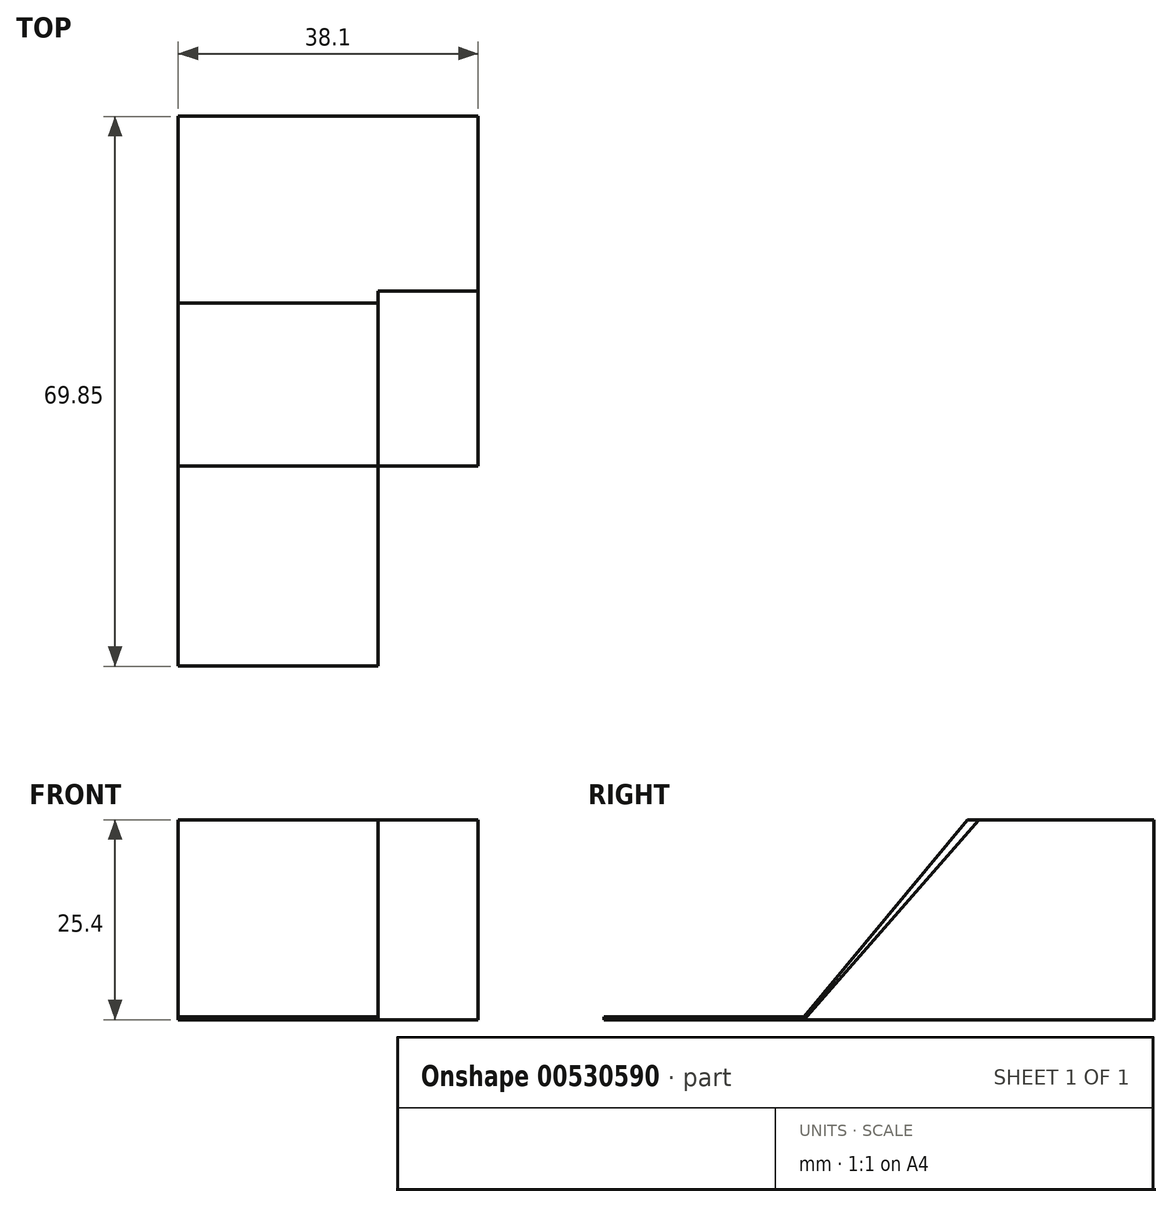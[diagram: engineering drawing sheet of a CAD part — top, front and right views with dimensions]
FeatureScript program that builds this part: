
annotation { "Feature Type Name" : "Feature", "Feature Type Description" : "" }
export const myFeature = defineFeature(function(context is Context, id is Id, definition is map)
    precondition{}
    {
        {
            var Q0;
            Q0=qCreatedBy(makeId("Top.planeOp"),FACE);
            var sketch = newSketch(context, id + "F0", { "sketchPlane" : qUnion([Q0])});
            skLineSegment(sketch, "E0", {"start": v(-52.88, 44.72) * mm, "end": v(-14.78, 44.72) * mm});
            skLineSegment(sketch, "E1", {"start": v(-14.78, 44.72) * mm, "end": v(-14.78, 25.67) * mm});
            skLineSegment(sketch, "E2", {"start": v(-14.78, 25.67) * mm, "end": v(-27.48, 25.67) * mm});
            skLineSegment(sketch, "E3", {"start": v(-27.48, 25.67) * mm, "end": v(-27.48, 0.27) * mm});
            skLineSegment(sketch, "E4", {"start": v(-27.48, 0.27) * mm, "end": v(-40.18, 0.27) * mm});
            skLineSegment(sketch, "E5", {"start": v(-40.18, 0.27) * mm, "end": v(-40.18, 25.67) * mm});
            skLineSegment(sketch, "E6", {"start": v(-40.18, 25.67) * mm, "end": v(-52.88, 25.67) * mm});
            skLineSegment(sketch, "E7", {"start": v(-52.88, 25.67) * mm, "end": v(-52.88, 44.72) * mm});
            skSolve(sketch);
        }
        {
            var Q0;
            Q0 = qSketchRegion(id + "F0", true);
            extrude(context, id + "F1", {"entities" : qUnion([Q0]), "depth" : 25.4 * mm, "offsetDistance" : 25.4 * mm});
        }
        {
            var Q0;
            Q0=makeQuery(id+"F1.opExtrude","SWEPT_FACE",FACE,{"disambiguationData":[OSD([sQuery(id+"F0.wireOp",EDGE,"E6")])]});
            extrude(context, id + "F2", {"entities" : qUnion([Q0]), "operationType" : NewBodyOperationType.ADD, "depth" : 25.4 * mm, "offsetDistance" : 25.4 * mm});
        }
        {
            var Q0;
            {var subQ0=sQuery(id+"F0.wireOp",EDGE,"E7");Q0=makeQuery(id+"F2.boolean.opBoolean","MERGE",FACE,{"derivedFrom":[makeQuery(id+"F1.opExtrude","SWEPT_FACE",FACE,{"disambiguationData":[OSD([subQ0])]}),makeQuery(id+"F2.opExtrude","SWEPT_FACE",FACE,{"disambiguationData":[OSD([sQuery(id+"F0.wireOp",EDGE,"E6"),subQ0])]})]});}
            var sketch = newSketch(context, id + "F3", { "sketchPlane" : qUnion([Q0])});
            skLineSegment(sketch, "E8", {"start": v(-21.03, 25.4) * mm, "end": v(0, 0) * mm});
            skSolve(sketch);
        }
        {
            var Q0;
            Q0 = qSketchRegion(id + "F3", true);
            var Q1;
            {var subQ0=sQuery(id+"F3.wireOp",EDGE,"E8");var subQ1=sQuery(id+"F0.wireOp",EDGE,"E7");var subQ2=sQuery(id+"F0.wireOp",EDGE,"E6");var subQ5=makeQuery(id+"F2.opExtrude","CAP_EDGE",EDGE,{"disambiguationData":[OSD([subQ2,subQ1])],"isStart":false});var subQ6=makeQuery(id+"F3.imprint","INTERSECT",VERTEX,{"derivedFrom":[subQ5,subQ0]});Q1=makeQuery(id+"F3.imprint","IMPRINT",FACE,{"disambiguationData":[TD([[makeQuery(id+"F3.imprint","IMPRINT",EDGE,{"disambiguationData":[TD([[subQ6,1.0]])],"derivedFrom":subQ0}),1.0]])]});}
            extrude(context, id + "F4", {"entities" : qUnion([Q0, Q1]), "operationType" : NewBodyOperationType.REMOVE, "oppositeDirection" : true, "depth" : 12.7 * mm, "offsetDistance" : 25.4 * mm});
        }
        {
            var Q0;
            Q0=makeQuery(id+"F2.boolean.opBoolean","MERGE",FACE,{"derivedFrom":[makeQuery(id+"F1.opExtrude","SWEPT_FACE",FACE,{"disambiguationData":[OSD([sQuery(id+"F0.wireOp",EDGE,"E4")])]}),makeQuery(id+"F2.opExtrude","CAP_FACE",FACE,{"disambiguationData":[OSD([sQuery(id+"F0.wireOp",EDGE,"E6")])],"isStart":false})]});
            extrude(context, id + "F5", {"entities" : qUnion([Q0]), "operationType" : NewBodyOperationType.ADD, "depth" : 25.4 * mm, "offsetDistance" : 25.4 * mm});
        }
        {
            var Q0;
            {var subQ0=sQuery(id+"F0.wireOp",EDGE,"E7");var subQ1=sQuery(id+"F0.wireOp",EDGE,"E6");var subQ2=makeQuery(id+"F2.opExtrude","CAP_EDGE",EDGE,{"disambiguationData":[OSD([subQ1,subQ0])],"isStart":false});var subQ3=sQuery(id+"F3.wireOp",EDGE,"E8");Q0=makeQuery(id+"F5.boolean.opBoolean","MERGE",FACE,{"derivedFrom":[makeQuery(id+"F4.boolean.opBoolean","COPY",FACE,{"derivedFrom":makeQuery(id+"F4.opExtrude","CAP_FACE",FACE,{"disambiguationData":[OSD([subQ1,subQ0,subQ3])],"isStart":false})}),makeQuery(id+"F5.opExtrude","SWEPT_FACE",FACE,{"disambiguationData":[OSD([subQ1,subQ0]),TDD([makeQuery(id+"F4.boolean.opBoolean","COPY",EDGE,{"derivedFrom":makeQuery(id+"F4.opExtrude","CAP_EDGE",EDGE,{"disambiguationData":[OSD([subQ1,subQ0]),TDD([makeQuery(id+"F3.imprint","IMPRINT",EDGE,{"disambiguationData":[TD([[makeQuery(id+"F3.imprint","INTERSECT",VERTEX,{"derivedFrom":[subQ2,subQ3]}),1.0]])],"derivedFrom":subQ2})])],"isStart":false})})])]})]});}
            var sketch = newSketch(context, id + "F6", { "sketchPlane" : qUnion([Q0])});
            skLineSegment(sketch, "E9", {"start": v(5.98, 25.4) * mm, "end": v(25.13, 0.33) * mm});
            skSolve(sketch);
        }
        {
            var Q0;
            {var subQ0=sQuery(id+"F6.wireOp",EDGE,"E9");Q0=makeQuery(id+"F6.imprint","IMPRINT",FACE,{"disambiguationData":[TD([[makeQuery(id+"F6.imprint","IMPRINT",EDGE,{"derivedFrom":subQ0}),1.0]])]});}
            extrude(context, id + "F7", {"entities" : qUnion([Q0]), "operationType" : NewBodyOperationType.REMOVE, "oppositeDirection" : true, "depth" : 25.4 * mm, "offsetDistance" : 25.4 * mm});
        }
        {
            var Q0;
            Q0=makeQuery(id+"F5.opExtrude","SWEPT_FACE",FACE,{"disambiguationData":[OSD([sQuery(id+"F0.wireOp",EDGE,"E6"),sQuery(id+"F0.wireOp",EDGE,"E7"),sQuery(id+"F3.wireOp",EDGE,"E8")])]});
            extrude(context, id + "F8", {"entities" : qUnion([Q0]), "operationType" : NewBodyOperationType.REMOVE, "oppositeDirection" : true, "depth" : 25.4 * mm, "offsetDistance" : 25.4 * mm});
        }
        {
            var Q0;
            Q0=makeQuery(id+"F1.opExtrude","SWEPT_FACE",FACE,{"disambiguationData":[OSD([sQuery(id+"F0.wireOp",EDGE,"E2")])]});
            extrude(context, id + "F9", {"entities" : qUnion([Q0]), "operationType" : NewBodyOperationType.ADD, "depth" : 25.4 * mm, "offsetDistance" : 25.4 * mm});
        }
        {
            var Q0;
            {var subQ0=sQuery(id+"F0.wireOp",EDGE,"E1");Q0=makeQuery(id+"F9.boolean.opBoolean","MERGE",FACE,{"derivedFrom":[makeQuery(id+"F1.opExtrude","SWEPT_FACE",FACE,{"disambiguationData":[OSD([subQ0])]}),makeQuery(id+"F9.opExtrude","SWEPT_FACE",FACE,{"disambiguationData":[OSD([subQ0,sQuery(id+"F0.wireOp",EDGE,"E2")])]})]});}
            var sketch = newSketch(context, id + "F10", { "sketchPlane" : qUnion([Q0])});
            skLineSegment(sketch, "E10", {"start": v(22.5, 25.4) * mm, "end": v(0.27, 0) * mm});
            skSolve(sketch);
        }
        {
            var Q0;
            {var subQ0=sQuery(id+"F10.wireOp",EDGE,"E10");Q0=makeQuery(id+"F10.imprint","IMPRINT",FACE,{"disambiguationData":[TD([[makeQuery(id+"F10.imprint","IMPRINT",EDGE,{"derivedFrom":subQ0}),-1.0]])]});}
            extrude(context, id + "F11", {"entities" : qUnion([Q0]), "operationType" : NewBodyOperationType.REMOVE, "oppositeDirection" : true, "depth" : 12.7 * mm, "offsetDistance" : 25.4 * mm});
        }
    });
